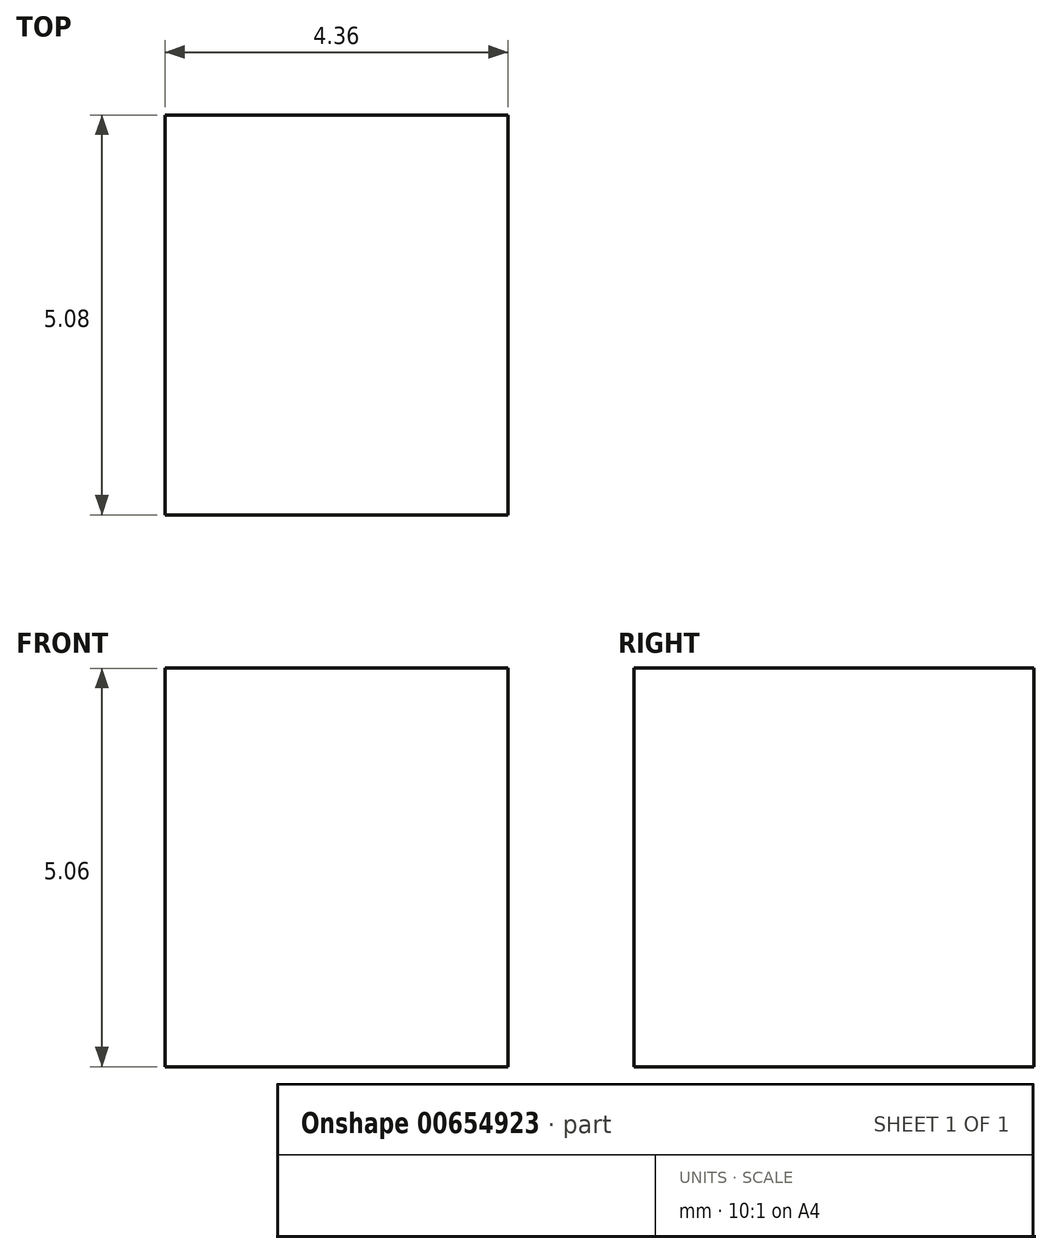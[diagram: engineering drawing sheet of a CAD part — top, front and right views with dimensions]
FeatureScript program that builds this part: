
annotation { "Feature Type Name" : "Feature", "Feature Type Description" : "" }
export const myFeature = defineFeature(function(context is Context, id is Id, definition is map)
    precondition{}
    {
        {
            var Q0;
            Q0=qCreatedBy(makeId("Front.planeOp"),FACE);
            var sketch = newSketch(context, id + "F0", { "sketchPlane" : qUnion([Q0])});
            skLineSegment(sketch, "E0", {"start": v(0, 0) * mm, "end": v(4.36, 0) * mm});
            skLineSegment(sketch, "E1", {"start": v(4.36, 0) * mm, "end": v(4.36, 5.06) * mm});
            skLineSegment(sketch, "E2", {"start": v(4.36, 5.06) * mm, "end": v(0, 5.06) * mm});
            skLineSegment(sketch, "E3", {"start": v(0, 5.06) * mm, "end": v(0, 0) * mm});
            skSolve(sketch);
        }
        {
            var Q0;
            Q0=makeQuery(id+"F0.imprint","IMPRINT",FACE,{"disambiguationData":[TD([[makeQuery(id+"F0.imprint","IMPRINT",EDGE,{"derivedFrom":sQuery(id+"F0.wireOp",EDGE,"E0")}),1.0]])]});
            extrude(context, id + "F1", {"entities" : qUnion([Q0]), "depth" : 5.08 * mm, "offsetDistance" : 25.4 * mm});
        }
    });
